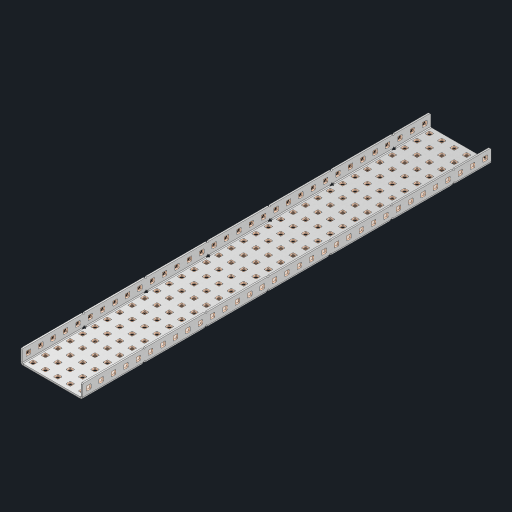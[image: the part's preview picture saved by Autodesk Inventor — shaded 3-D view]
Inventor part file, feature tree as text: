
AUTODESK INVENTOR PART (.ipt)
format: ipt  version: 2023 (Build 270158000, 158)  size: 2,440,192 bytes
history: native  units: in
note: dims shown in document units (in); Inventor stores cm internally (conversion verified against a paired STEP export)
features: other x236, extrude x230, sheet_metal_op x10, sketch x8, mirror x1, pattern_linear x1, chamfer x1
ambient origin geometry x8: Origin, YZ Plane, XZ Plane, XY Plane, X Axis, Y Axis, Z Axis, Center Point
bodies: Solid1 (feature_tree), Body (feature_tree)
feature tree (487):
  other  "Flange Pattern Plane"
  sheet_metal_op  "Flange Pattern"
  sheet_metal_op  "Body Pattern"
  other  "Arc Length"
  mirror  "Notch Mirror"
  pattern_linear  "Notch Pattern"  Spacing1=0.25in  [1 undecoded]
  chamfer  "End Chamfer"
  extrude  "Half Cut"  Depth=0.0625in
  sketch  "Sketch1"  dims[d0=2.5in]
  other  "Plate1"
  sketch  "Sketch2"  dims[d1=16.5in]
  other  "Plate2"
  sheet_metal_op  "Bend1"
  sheet_metal_op  "Corner1"
  sketch  "Sketch3"  dims[d2=0.0625in]
  other  "Flange Pattern Sketch"
  sketch  "Sketch7"  dims[d3=0.0625in]
  other  "Srf1"
  other  "Srf2"
  sketch  "Sketch8"  dims[d4=0.0312in]
  sketch  "Sketch9"  dims[d5=0.125in]
  other  "Srf91"
  sheet_metal_op  "Body Pattern Sketch"
  other  "Srf92"
  sketch  "Sketch13"  dims[d6=0.0625in]
  sketch  "Sketch14"  dims[d7=0.5in d8=90.0deg d9=0.0312in d10=0.25in d11=0.0625in d12=0.0625in d16=0.182in d17=0.02in d18=0.0625in d19=0.0in d20=0.25in d21=0.25in d46=0.172in d47=1.0in d48=0.0in d49=0.182in d50=0.02in d51=0.25in d52=0.25in d53=0.0625in d54=0.0in d55=0.172in d56=1.0in d57=0.0in d60=12.9921in d62=0.5in d63=1.9685in d65=0.5in d85=0.1473in d86=0.1782in d88=0.04in d89=0.0625in d90=0.0in d91=0.04in d92=0.0491in d95=2.5in d96=0.04in d97=0.25in d98=45.0deg d101=0.0in d102=2.497in d131=2.5in d132=12.9921in d134=0.5in d139=0.5in]
  other  "Srf856"
  other  "Srf1310"
  other  "Srf1311"
  other  "Srf1312"
  other  "Srf1376"
  other  "Srf1377"
  other  "Srf1728"
  other  "Srf1755"
  other  "Srf1878"
  other  "Srf1879"
  other  "Srf1880"
  other  "Srf1881"
  other  "Srf1882"
  other  "Srf1883"
  other  "Srf1884"
  other  "Srf1885"
  other  "Srf1886"
  other  "Srf1887"
  other  "Srf1888"
  other  "Srf1889"
  other  "Srf1890"
  other  "Srf1891"
  other  "Srf1892"
  other  "Srf1893"
  other  "Srf1894"
  other  "Srf1895"
  other  "Srf1896"
  other  "Srf1897"
  other  "Srf1898"
  other  "Srf1899"
  other  "Srf1900"
  other  "Srf1901"
  other  "Srf1902"
  other  "Srf1903"
  other  "Srf1904"
  other  "Srf1905"
  other  "Srf1906"
  other  "Srf1942"
  other  "Srf1943"
  other  "Srf1944"
  other  "Srf1945"
  other  "Srf1946"
  other  "Srf1947"
  other  "Srf1948"
  other  "Srf1949"
  other  "Srf1950"
  other  "Srf1951"
  other  "Srf1952"
  other  "Srf1953"
  other  "Srf1954"
  other  "Srf1955"
  other  "Srf1956"
  other  "Srf1957"
  other  "Srf1958"
  other  "Srf1959"
  other  "Srf1960"
  other  "Srf1961"
  other  "Srf1962"
  other  "Srf1963"
  other  "Srf1964"
  other  "Srf1965"
  other  "Srf1966"
  other  "Srf1967"
  other  "Srf1968"
  other  "Srf1969"
  other  "Srf1970"
  other  "Srf2111"
  other  "Srf2112"
  other  "Srf2113"
  other  "Srf2114"
  other  "Srf2115"
  other  "Srf2116"
  other  "Srf2117"
  other  "Srf2118"
  other  "Srf2119"
  other  "Srf2120"
  other  "Srf2121"
  other  "Srf2122"
  other  "Srf2123"
  other  "Srf2124"
  other  "Srf2125"
  other  "Srf2126"
  other  "Srf2127"
  other  "Srf2128"
  other  "Srf2129"
  other  "Srf2130"
  other  "Srf2131"
  other  "Srf2132"
  other  "Srf2133"
  other  "Srf2134"
  other  "Srf2135"
  other  "Srf2136"
  other  "Srf2137"
  other  "Srf2138"
  other  "Srf2139"
  other  "Srf2140"
  other  "Srf2141"
  other  "Srf2146"
  other  "Srf2147"
  other  "Srf2148"
  other  "Srf2149"
  other  "Srf2150"
  other  "Srf2151"
  other  "Srf2152"
  other  "Srf2153"
  other  "Srf2154"
  other  "Srf2155"
  other  "Srf2156"
  other  "Srf2157"
  other  "Srf2158"
  other  "Srf2159"
  other  "Srf2160"
  other  "Srf2161"
  other  "Srf2162"
  other  "Srf2163"
  other  "Srf2164"
  other  "Srf2165"
  other  "Srf2166"
  other  "Srf2167"
  other  "Srf2168"
  other  "Srf2169"
  other  "Srf2170"
  other  "Srf2171"
  other  "Srf2172"
  other  "Srf2173"
  other  "Srf2174"
  other  "Srf2175"
  other  "Srf2176"
  other  "Srf2177"
  other  "Srf2178"
  other  "Srf2179"
  other  "Srf2180"
  other  "Srf2181"
  other  "Srf2182"
  other  "Srf2183"
  other  "Srf2184"
  other  "Srf2185"
  other  "Srf2186"
  other  "Srf2187"
  other  "Srf2188"
  other  "Srf2189"
  other  "Srf2190"
  other  "Srf2191"
  other  "Srf2192"
  other  "Srf2193"
  other  "Srf2194"
  other  "Srf2195"
  other  "Srf2196"
  other  "Srf2197"
  other  "Srf2198"
  other  "Srf2199"
  other  "Srf2200"
  other  "Srf2201"
  other  "Srf2202"
  other  "Srf2203"
  other  "Srf2204"
  other  "Srf2205"
  other  "Srf2206"
  other  "Srf2207"
  other  "Srf2208"
  other  "Srf2209"
  other  "Srf2210"
  other  "Srf2211"
  other  "Srf2212"
  other  "Srf2213"
  other  "Srf2214"
  other  "Srf2215"
  other  "Srf2216"
  other  "Srf2217"
  other  "Srf2218"
  other  "Srf2219"
  other  "Srf2220"
  other  "Srf2221"
  other  "Srf2222"
  other  "Srf2223"
  other  "Srf2224"
  other  "Srf2225"
  other  "Srf2226"
  other  "Srf2227"
  other  "Srf2228"
  other  "Srf2229"
  other  "Srf2230"
  other  "Srf2231"
  other  "Srf2232"
  other  "Srf2233"
  other  "Srf2234"
  other  "Srf2235"
  other  "Srf2236"
  other  "Srf2237"
  other  "Srf2238"
  other  "Srf2239"
  other  "Srf2240"
  other  "Srf2241"
  other  "Srf2242"
  other  "Srf2243"
  other  "Srf2244"
  other  "Srf2245"
  other  "Srf2246"
  other  "Srf2247"
  other  "Srf2248"
  other  "Srf2249"
  other  "Srf2250"
  other  "Srf2251"
  other  "Srf2252"
  other  "Srf2253"
  other  "Srf2254"
  other  "Srf2255"
  other  "Srf2256"
  other  "Srf2257"
  other  "Srf2258"
  other  "Srf2259"
  other  "Srf2260"
  other  "Srf2261"
  other  "Srf2262"
  other  "Srf2263"
  other  "Srf2264"
  other  "Srf2265"
  other  "Srf2266"
  other  "Srf2267"
  other  "Srf2268"
  other  "Srf2269"
  other  "Srf2270"
  other  "Srf2271"
  other  "Srf2272"
  other  "Srf2273"
  other  "Srf2274"
  other  "Srf2275"
  sheet_metal_op  "Flange Stamp"
  sheet_metal_op  "Flange Circle"
  sheet_metal_op  "Body Stamp"
  sheet_metal_op  "Body Circle"
  sheet_metal_op  "Notch"
  extrude  "ExtrusionSrf2"  Depth=0.0625in
  extrude  "ExtrusionSrf92"  Depth=2.5in
  extrude  "ExtrusionSrf856"  Depth=0.02in
  extrude  "ExtrusionSrf1310"  Depth=0.0625in
  extrude  "ExtrusionSrf1311"  TaperAngle=0.0deg  [1 undecoded]
  extrude  "ExtrusionSrf1312"  Depth=0.25in
  extrude  "ExtrusionSrf1376"  Depth=0.25in
  extrude  "ExtrusionSrf1377"  Depth=2.5in
  extrude  "ExtrusionSrf1728"  Depth=2.5in TaperAngle=0.0deg
  extrude  "ExtrusionSrf1755"  Depth=2.5in
  extrude  "ExtrusionSrf1878"  Depth=0.02in
  extrude  "ExtrusionSrf1879"  Depth=0.25in
  extrude  "ExtrusionSrf1880"  Depth=0.25in
  extrude  "ExtrusionSrf1881"  Depth=0.0625in
  extrude  "ExtrusionSrf1882"  TaperAngle=0.0deg  [1 undecoded]
  extrude  "ExtrusionSrf1883"  Depth=2.5in
  extrude  "ExtrusionSrf1884"  Depth=2.5in TaperAngle=0.0deg
  extrude  "ExtrusionSrf1885"  Depth=2.5in
  extrude  "ExtrusionSrf1886"  Depth=2.5in
  extrude  "ExtrusionSrf1887"  Depth=2.5in
  extrude  "ExtrusionSrf1888"  Depth=2.5in
  extrude  "ExtrusionSrf1889"  Depth=2.5in
  extrude  "ExtrusionSrf1890"  Depth=0.0625in
  extrude  "ExtrusionSrf1891"  TaperAngle=0.0deg  [1 undecoded]
  extrude  "ExtrusionSrf1892"  Depth=2.5in
  extrude  "ExtrusionSrf1893"  Depth=2.5in
  extrude  "ExtrusionSrf1894"  Depth=2.5in
  extrude  "ExtrusionSrf1895"  Depth=0.25in TaperAngle=45.0deg
  extrude  "ExtrusionSrf1896"  TaperAngle=0.0deg  [1 undecoded]
  extrude  "ExtrusionSrf1897"  Depth=2.5in
  extrude  "ExtrusionSrf1898"  Depth=2.5in
  extrude  "ExtrusionSrf1899"  Depth=2.5in
  extrude  "ExtrusionSrf1900"  Depth=2.5in
  extrude  "ExtrusionSrf1901"  Depth=2.5in
  extrude  "ExtrusionSrf1902"  [1 undecoded]
  extrude  "ExtrusionSrf1903"  [1 undecoded]
  extrude  "ExtrusionSrf1904"  [1 undecoded]
  extrude  "ExtrusionSrf1905"  [1 undecoded]
  extrude  "ExtrusionSrf1906"  [1 undecoded]
  extrude  "ExtrusionSrf1942"  [1 undecoded]
  extrude  "ExtrusionSrf1943"  [1 undecoded]
  extrude  "ExtrusionSrf1944"  [1 undecoded]
  extrude  "ExtrusionSrf1945"  [1 undecoded]
  extrude  "ExtrusionSrf1946"  [1 undecoded]
  extrude  "ExtrusionSrf1947"  [1 undecoded]
  extrude  "ExtrusionSrf1948"  [1 undecoded]
  extrude  "ExtrusionSrf1949"  [1 undecoded]
  extrude  "ExtrusionSrf1950"  [1 undecoded]
  extrude  "ExtrusionSrf1951"  [1 undecoded]
  extrude  "ExtrusionSrf1952"  [1 undecoded]
  extrude  "ExtrusionSrf1953"  [1 undecoded]
  extrude  "ExtrusionSrf1954"  [1 undecoded]
  extrude  "ExtrusionSrf1955"  [1 undecoded]
  extrude  "ExtrusionSrf1956"  [1 undecoded]
  extrude  "ExtrusionSrf1957"  [1 undecoded]
  extrude  "ExtrusionSrf1958"  [1 undecoded]
  extrude  "ExtrusionSrf1959"  [1 undecoded]
  extrude  "ExtrusionSrf1960"  [1 undecoded]
  extrude  "ExtrusionSrf1961"  [1 undecoded]
  extrude  "ExtrusionSrf1962"  [1 undecoded]
  extrude  "ExtrusionSrf1963"  [1 undecoded]
  extrude  "ExtrusionSrf1964"  [1 undecoded]
  extrude  "ExtrusionSrf1965"  [1 undecoded]
  extrude  "ExtrusionSrf1966"  [1 undecoded]
  extrude  "ExtrusionSrf1967"  [1 undecoded]
  extrude  "ExtrusionSrf1968"  [1 undecoded]
  extrude  "ExtrusionSrf1969"  [1 undecoded]
  extrude  "ExtrusionSrf1970"  [1 undecoded]
  extrude  "ExtrusionSrf2111"  [1 undecoded]
  extrude  "ExtrusionSrf2112"  [1 undecoded]
  extrude  "ExtrusionSrf2113"  [1 undecoded]
  extrude  "ExtrusionSrf2114"  [1 undecoded]
  extrude  "ExtrusionSrf2115"  [1 undecoded]
  extrude  "ExtrusionSrf2116"  [1 undecoded]
  extrude  "ExtrusionSrf2117"  [1 undecoded]
  extrude  "ExtrusionSrf2118"  [1 undecoded]
  extrude  "ExtrusionSrf2119"  [1 undecoded]
  extrude  "ExtrusionSrf2120"  [1 undecoded]
  extrude  "ExtrusionSrf2121"  [1 undecoded]
  extrude  "ExtrusionSrf2122"  [1 undecoded]
  extrude  "ExtrusionSrf2123"  [1 undecoded]
  extrude  "ExtrusionSrf2124"  [1 undecoded]
  extrude  "ExtrusionSrf2125"  [1 undecoded]
  extrude  "ExtrusionSrf2126"  [1 undecoded]
  extrude  "ExtrusionSrf2127"  [1 undecoded]
  extrude  "ExtrusionSrf2128"  [1 undecoded]
  extrude  "ExtrusionSrf2129"  [1 undecoded]
  extrude  "ExtrusionSrf2130"  [1 undecoded]
  extrude  "ExtrusionSrf2131"  [1 undecoded]
  extrude  "ExtrusionSrf2132"  [1 undecoded]
  extrude  "ExtrusionSrf2133"  [1 undecoded]
  extrude  "ExtrusionSrf2134"  [1 undecoded]
  extrude  "ExtrusionSrf2135"  [1 undecoded]
  extrude  "ExtrusionSrf2136"  [1 undecoded]
  extrude  "ExtrusionSrf2137"  [1 undecoded]
  extrude  "ExtrusionSrf2138"  [1 undecoded]
  extrude  "ExtrusionSrf2139"  [1 undecoded]
  extrude  "ExtrusionSrf2140"  [1 undecoded]
  extrude  "ExtrusionSrf2141"  [1 undecoded]
  extrude  "ExtrusionSrf2146"  [1 undecoded]
  extrude  "ExtrusionSrf2147"  [1 undecoded]
  extrude  "ExtrusionSrf2148"  [1 undecoded]
  extrude  "ExtrusionSrf2149"  [1 undecoded]
  extrude  "ExtrusionSrf2150"  [1 undecoded]
  extrude  "ExtrusionSrf2151"  [1 undecoded]
  extrude  "ExtrusionSrf2152"  [1 undecoded]
  extrude  "ExtrusionSrf2153"  [1 undecoded]
  extrude  "ExtrusionSrf2154"  [1 undecoded]
  extrude  "ExtrusionSrf2155"  [1 undecoded]
  extrude  "ExtrusionSrf2156"  [1 undecoded]
  extrude  "ExtrusionSrf2157"  [1 undecoded]
  extrude  "ExtrusionSrf2158"  [1 undecoded]
  extrude  "ExtrusionSrf2159"  [1 undecoded]
  extrude  "ExtrusionSrf2160"  [1 undecoded]
  extrude  "ExtrusionSrf2161"  [1 undecoded]
  extrude  "ExtrusionSrf2162"  [1 undecoded]
  extrude  "ExtrusionSrf2163"  [1 undecoded]
  extrude  "ExtrusionSrf2164"  [1 undecoded]
  extrude  "ExtrusionSrf2165"  [1 undecoded]
  extrude  "ExtrusionSrf2166"  [1 undecoded]
  extrude  "ExtrusionSrf2167"  [1 undecoded]
  extrude  "ExtrusionSrf2168"  [1 undecoded]
  extrude  "ExtrusionSrf2169"  [1 undecoded]
  extrude  "ExtrusionSrf2170"  [1 undecoded]
  extrude  "ExtrusionSrf2171"  [1 undecoded]
  extrude  "ExtrusionSrf2172"  [1 undecoded]
  extrude  "ExtrusionSrf2173"  [1 undecoded]
  extrude  "ExtrusionSrf2174"  [1 undecoded]
  extrude  "ExtrusionSrf2175"  [1 undecoded]
  extrude  "ExtrusionSrf2176"  [1 undecoded]
  extrude  "ExtrusionSrf2177"  [1 undecoded]
  extrude  "ExtrusionSrf2178"  [1 undecoded]
  extrude  "ExtrusionSrf2179"  [1 undecoded]
  extrude  "ExtrusionSrf2180"  [1 undecoded]
  extrude  "ExtrusionSrf2181"  [1 undecoded]
  extrude  "ExtrusionSrf2182"  [1 undecoded]
  extrude  "ExtrusionSrf2183"  [1 undecoded]
  extrude  "ExtrusionSrf2184"  [1 undecoded]
  extrude  "ExtrusionSrf2185"  [1 undecoded]
  extrude  "ExtrusionSrf2186"  [1 undecoded]
  extrude  "ExtrusionSrf2187"  [1 undecoded]
  extrude  "ExtrusionSrf2188"  [1 undecoded]
  extrude  "ExtrusionSrf2189"  [1 undecoded]
  extrude  "ExtrusionSrf2190"  [1 undecoded]
  extrude  "ExtrusionSrf2191"  [1 undecoded]
  extrude  "ExtrusionSrf2192"  [1 undecoded]
  extrude  "ExtrusionSrf2193"  [1 undecoded]
  extrude  "ExtrusionSrf2194"  [1 undecoded]
  extrude  "ExtrusionSrf2195"  [1 undecoded]
  extrude  "ExtrusionSrf2196"  [1 undecoded]
  extrude  "ExtrusionSrf2197"  [1 undecoded]
  extrude  "ExtrusionSrf2198"  [1 undecoded]
  extrude  "ExtrusionSrf2199"  [1 undecoded]
  extrude  "ExtrusionSrf2200"  [1 undecoded]
  extrude  "ExtrusionSrf2201"  [1 undecoded]
  extrude  "ExtrusionSrf2202"  [1 undecoded]
  extrude  "ExtrusionSrf2203"  [1 undecoded]
  extrude  "ExtrusionSrf2204"  [1 undecoded]
  extrude  "ExtrusionSrf2205"  [1 undecoded]
  extrude  "ExtrusionSrf2206"  [1 undecoded]
  extrude  "ExtrusionSrf2207"  [1 undecoded]
  extrude  "ExtrusionSrf2208"  [1 undecoded]
  extrude  "ExtrusionSrf2209"  [1 undecoded]
  extrude  "ExtrusionSrf2210"  [1 undecoded]
  extrude  "ExtrusionSrf2211"  [1 undecoded]
  extrude  "ExtrusionSrf2212"  [1 undecoded]
  extrude  "ExtrusionSrf2213"  [1 undecoded]
  extrude  "ExtrusionSrf2214"  [1 undecoded]
  extrude  "ExtrusionSrf2215"  [1 undecoded]
  extrude  "ExtrusionSrf2216"  [1 undecoded]
  extrude  "ExtrusionSrf2217"  [1 undecoded]
  extrude  "ExtrusionSrf2218"  [1 undecoded]
  extrude  "ExtrusionSrf2219"  [1 undecoded]
  extrude  "ExtrusionSrf2220"  [1 undecoded]
  extrude  "ExtrusionSrf2221"  [1 undecoded]
  extrude  "ExtrusionSrf2222"  [1 undecoded]
  extrude  "ExtrusionSrf2223"  [1 undecoded]
  extrude  "ExtrusionSrf2224"  [1 undecoded]
  extrude  "ExtrusionSrf2225"  [1 undecoded]
  extrude  "ExtrusionSrf2226"  [1 undecoded]
  extrude  "ExtrusionSrf2227"  [1 undecoded]
  extrude  "ExtrusionSrf2228"  [1 undecoded]
  extrude  "ExtrusionSrf2229"  [1 undecoded]
  extrude  "ExtrusionSrf2230"  [1 undecoded]
  extrude  "ExtrusionSrf2231"  [1 undecoded]
  extrude  "ExtrusionSrf2232"  [1 undecoded]
  extrude  "ExtrusionSrf2233"  [1 undecoded]
  extrude  "ExtrusionSrf2234"  [1 undecoded]
  extrude  "ExtrusionSrf2235"  [1 undecoded]
  extrude  "ExtrusionSrf2236"  [1 undecoded]
  extrude  "ExtrusionSrf2237"  [1 undecoded]
  extrude  "ExtrusionSrf2238"  [1 undecoded]
  extrude  "ExtrusionSrf2239"  [1 undecoded]
  extrude  "ExtrusionSrf2240"  [1 undecoded]
  extrude  "ExtrusionSrf2241"  [1 undecoded]
  extrude  "ExtrusionSrf2242"  [1 undecoded]
  extrude  "ExtrusionSrf2243"  [1 undecoded]
  extrude  "ExtrusionSrf2244"  [1 undecoded]
  extrude  "ExtrusionSrf2245"  [1 undecoded]
  extrude  "ExtrusionSrf2246"  [1 undecoded]
  extrude  "ExtrusionSrf2247"  [1 undecoded]
  extrude  "ExtrusionSrf2248"  [1 undecoded]
  extrude  "ExtrusionSrf2249"  [1 undecoded]
  extrude  "ExtrusionSrf2250"  [1 undecoded]
  extrude  "ExtrusionSrf2251"  [1 undecoded]
  extrude  "ExtrusionSrf2252"  [1 undecoded]
  extrude  "ExtrusionSrf2253"  [1 undecoded]
  extrude  "ExtrusionSrf2254"  [1 undecoded]
  extrude  "ExtrusionSrf2255"  [1 undecoded]
  extrude  "ExtrusionSrf2256"  [1 undecoded]
  extrude  "ExtrusionSrf2257"  [1 undecoded]
  extrude  "ExtrusionSrf2258"  [1 undecoded]
  extrude  "ExtrusionSrf2259"  [1 undecoded]
  extrude  "ExtrusionSrf2260"  [1 undecoded]
  extrude  "ExtrusionSrf2261"  [1 undecoded]
  extrude  "ExtrusionSrf2262"  [1 undecoded]
  extrude  "ExtrusionSrf2263"  [1 undecoded]
  extrude  "ExtrusionSrf2264"  [1 undecoded]
  extrude  "ExtrusionSrf2265"  [1 undecoded]
  extrude  "ExtrusionSrf2266"  [1 undecoded]
  extrude  "ExtrusionSrf2267"  [1 undecoded]
  extrude  "ExtrusionSrf2268"  [1 undecoded]
  extrude  "ExtrusionSrf2269"  [1 undecoded]
  extrude  "ExtrusionSrf2270"  [1 undecoded]
  extrude  "ExtrusionSrf2271"  [1 undecoded]
  extrude  "ExtrusionSrf2272"  [1 undecoded]
  extrude  "ExtrusionSrf2273"  [1 undecoded]
  extrude  "ExtrusionSrf2274"  [1 undecoded]
  extrude  "ExtrusionSrf2275"  [1 undecoded]
note: 200 required parameter values undecoded (feature->parameter linkage not recoverable at this tier; creation-order binding heuristic only, values carry confidence <= 0.55)
